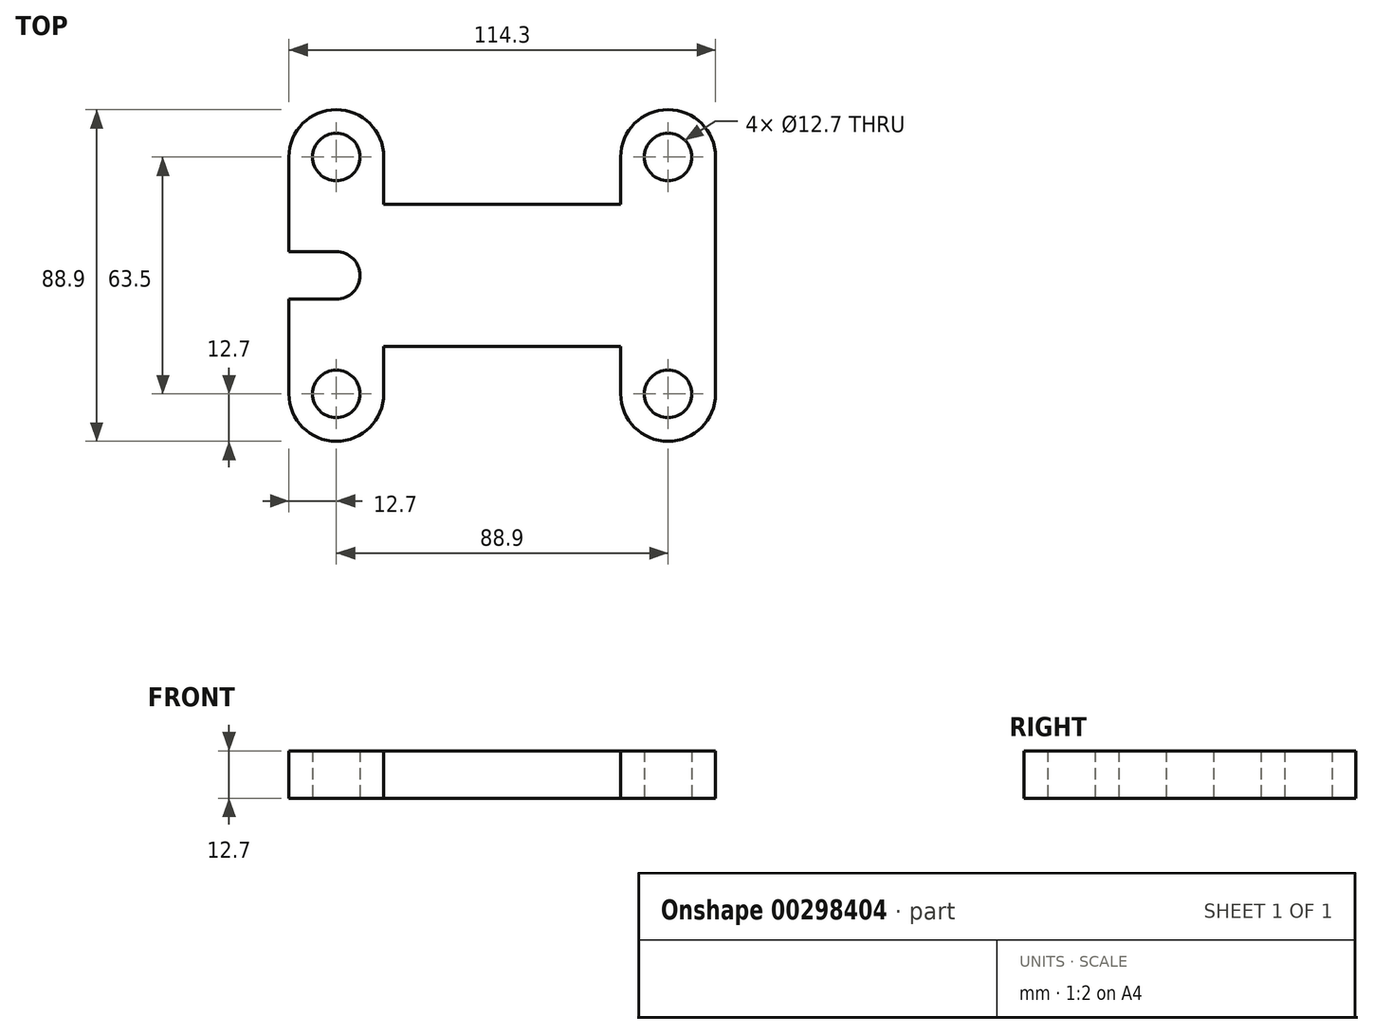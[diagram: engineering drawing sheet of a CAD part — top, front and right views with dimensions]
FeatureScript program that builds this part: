
annotation { "Feature Type Name" : "Feature", "Feature Type Description" : "" }
export const myFeature = defineFeature(function(context is Context, id is Id, definition is map)
    precondition{}
    {
        {
            var Q0;
            Q0=qCreatedBy(makeId("Top.planeOp"),FACE);
            var sketch = newSketch(context, id + "F0", { "sketchPlane" : qUnion([Q0])});
            skCircle(sketch, "E0", {"center": v(88.9, 63.5) * mm, "radius": 6.35 * mm});
            skCircle(sketch, "E1", {"center": v(88.9, 0) * mm, "radius": 6.35 * mm});
            skCircle(sketch, "E2", {"center": v(0, 0) * mm, "radius": 6.35 * mm});
            skCircle(sketch, "E3", {"center": v(0, 63.5) * mm, "radius": 6.35 * mm});
            skArc(sketch, "E4", {"start": v(88.9, -12.7) * mm, "mid": v(79.92, -8.98) * mm, "end": v(76.2, 0) * mm});
            skArc(sketch, "E5", {"start": v(88.9, -12.7) * mm, "mid": v(97.88, -8.98) * mm, "end": v(101.6, 0) * mm});
            skArc(sketch, "E6", {"start": v(88.9, 76.2) * mm, "mid": v(79.92, 72.48) * mm, "end": v(76.2, 63.5) * mm});
            skArc(sketch, "E7", {"start": v(88.9, 76.2) * mm, "mid": v(97.88, 72.48) * mm, "end": v(101.6, 63.5) * mm});
            skArc(sketch, "E8", {"start": v(0, -12.7) * mm, "mid": v(8.98, -8.98) * mm, "end": v(12.7, 0) * mm});
            skArc(sketch, "E9", {"start": v(0, -12.7) * mm, "mid": v(-8.98, -8.98) * mm, "end": v(-12.7, 0) * mm});
            skArc(sketch, "E10", {"start": v(0, 76.2) * mm, "mid": v(8.98, 72.48) * mm, "end": v(12.7, 63.5) * mm});
            skArc(sketch, "E11", {"start": v(0, 76.2) * mm, "mid": v(-8.98, 72.48) * mm, "end": v(-12.7, 63.5) * mm});
            skLineSegment(sketch, "E12", {"start": v(101.6, 63.5) * mm, "end": v(101.6, 50.8) * mm});
            skLineSegment(sketch, "E13", {"start": v(76.2, 50.8) * mm, "end": v(76.2, 63.5) * mm});
            skLineSegment(sketch, "E14", {"start": v(12.7, 63.5) * mm, "end": v(12.7, 50.8) * mm});
            skLineSegment(sketch, "E15", {"start": v(-12.7, 50.8) * mm, "end": v(-12.7, 63.5) * mm});
            skLineSegment(sketch, "E16", {"start": v(-12.7, 0) * mm, "end": v(-12.7, 12.7) * mm});
            skLineSegment(sketch, "E17", {"start": v(12.7, 12.7) * mm, "end": v(12.7, 0) * mm});
            skLineSegment(sketch, "E18", {"start": v(76.2, 0) * mm, "end": v(76.2, 12.7) * mm});
            skLineSegment(sketch, "E19", {"start": v(101.6, 12.7) * mm, "end": v(101.6, 0) * mm});
            skLineSegment(sketch, "E20.bottom", {"start": v(12.7, 50.8) * mm, "end": v(76.2, 50.8) * mm});
            skLineSegment(sketch, "E20.top", {"start": v(12.7, 12.7) * mm, "end": v(76.2, 12.7) * mm});
            skLineSegment(sketch, "E20.left", {"start": v(-12.7, 50.8) * mm, "end": v(-12.7, 38.1) * mm});
            skLineSegment(sketch, "E20.right", {"start": v(101.6, 50.8) * mm, "end": v(101.6, 12.7) * mm});
            skPoint(sketch, "E21", {"position": v(0, 31.75) * mm});
            skArc(sketch, "E22", {"start": v(6.35, 31.75) * mm, "mid": v(4.5, 36.24) * mm, "end": v(0, 38.1) * mm});
            skArc(sketch, "E23", {"start": v(6.35, 31.75) * mm, "mid": v(4.5, 27.26) * mm, "end": v(0, 25.4) * mm});
            skLineSegment(sketch, "E24", {"start": v(0, 38.1) * mm, "end": v(-12.7, 38.1) * mm});
            skLineSegment(sketch, "E25", {"start": v(0, 25.4) * mm, "end": v(-12.7, 25.4) * mm});
            skLineSegment(sketch, "E26.trimOffspring", {"start": v(-12.7, 25.4) * mm, "end": v(-12.7, 12.7) * mm});
            skSolve(sketch);
        }
        {
            var Q0;
            Q0 = qSketchRegion(id + "F0", true);
            extrude(context, id + "F1", {"entities" : qUnion([Q0]), "depth" : 12.7 * mm});
        }
    });
